# Revit family: Legrand Cabinet Plexo³ 4-8 modules
name_source: partatom
category: Equipement électrique
revit_build: Autodesk Revit 2018 (Build: 20170223_1515(x64)
units: mm (PartAtom-declared; Revit-internal decimal feet)

## family parameters
Basée sur le plan de construction = Non
Configuration du panneau = Deux colonnes, circuits au sein
Cote de connecteur circulaire = Utiliser le diamètre
Couper avec des vides une fois chargée = Non
Numéro OmniClass = 23.80.30.11.17
Partagée = Non
Point de calcul de pièce = Non
Titre OmniClass = Distribution Boards and Control Panels
Toujours verticalement = Oui
Type d'élément = Tableau de raccordement

## types (13) — shared parameters
ETIM Class 6.0 = EC000214
Fabricant = Legrand
General Conditions of Use = https://export.legrand.com
IK = 09
IP = 65
Material = Polystyrene
RAL = 7046
URL = www.legrand.fr

## per-type parameters (varying)
| type | Cabinet 001904 | Cabinet 001906 | Cabinet 001908 | Cabinet 601954 | Cabinet 601956 | Cabinet 601958 | Cabinet 601974 | Cabinet 601976 | Cabinet 601978 | Cabinet 601994 | Cabinet 601996 | Cabinet 601998 | Description | Image du type | Terminal block E | Terminal block N |
| Plexo³ 4 modules 1 row  001904 | Oui | Non | Non | Non | Non | Non | Non | Non | Non | Non | Non | Non | Plexo³ 4 modules 1 row  001904 | plexo3_6modules_001906_pw_182611_pz_4.jpg |  |  |
| Plexo³ 6 modules 1 row  001906 | Non | Oui | Non | Non | Non | Non | Non | Non | Non | Non | Non | Non | Plexo³ 6 modules 1 row  001906 | plexo3_6modules_001906_pw_182611_pz_4.jpg | terminal block 1+6 holes |  |
| Plexo³ 8 modules 1 row  001908 | Non | Non | Oui | Non | Non | Non | Non | Non | Non | Non | Non | Non | Plexo³ 8 modules 1 row  001908 | <Aucun> | terminal block 1+6 holes |  |
| Plexo³ 4 modules 1 row  601954 | Non | Non | Non | Oui | Non | Non | Non | Non | Non | Non | Non | Non | Plexo³ 4 modules 1 row  601954 | plexo3_6modules_001906_pw_182611_pz_4.jpg |  |  |
| Plexo³ 4 modules 1 row  601974 | Non | Non | Non | Non | Non | Non | Oui | Non | Non | Non | Non | Non | Plexo³ 4 modules 1 row  601974 | plexo3_6modules_001906_pw_182611_pz_4.jpg | terminal block 4 holes | terminal block 4 holes |
| Plexo³ 4 modules 1 row  601996 | Non | Non | Non | Non | Non | Non | Non | Non | Non | Non | Oui | Non | Plexo³ 4 modules 1 row  601996 | plexo3_6modules_001906_pw_182611_pz_4.jpg |  |  |
| Plexo³ 6 modules 1 row  601956 | Non | Non | Non | Non | Oui | Non | Non | Non | Non | Non | Non | Non | Plexo³ 6 modules 1 row  601956 | plexo3_6modules_001906_pw_182611_pz_4.jpg |  |  |
| Plexo³ 6 modules 1 row  601976 | Non | Non | Non | Non | Non | Non | Non | Oui | Non | Non | Non | Non | Plexo³ 6 modules 1 row  601976 | plexo3_6modules_001906_pw_182611_pz_4.jpg | terminal block 4 holes | terminal block 4 holes |
| Plexo³ 8 modules 1 row  601958 | Non | Non | Non | Non | Non | Oui | Non | Non | Non | Non | Non | Non | Plexo³ 8 modules 1 row  601958 | <Aucun> |  |  |
| Plexo³ 8 modules 1 row  601978 | Non | Non | Non | Non | Non | Non | Non | Non | Oui | Non | Non | Non | Plexo³ 8 modules 1 row  601978 | <Aucun> | terminal block 8 holes | terminal block 8 holes |
| Plexo³ 8 modules 1 row  601998 | Non | Non | Non | Non | Non | Non | Non | Non | Non | Non | Non | Oui | Plexo³ 8 modules 1 row  601978 | <Aucun> | terminal block 8 holes | terminal block 8 holes |
| Plexo³ 8 modules 1 row  601996 | Non | Non | Non | Non | Non | Non | Non | Non | Non | Non | Oui | Non | Plexo³ 6 modules 1 row  601996 | <Aucun> | terminal block 8 holes | terminal block 8 holes |
| Plexo³ 8 modules 1 row  601994 | Non | Non | Non | Non | Non | Non | Non | Non | Non | Oui | Non | Non | Plexo³ 4 modules 1 row  601994 | <Aucun> | terminal block 8 holes | terminal block 8 holes |
